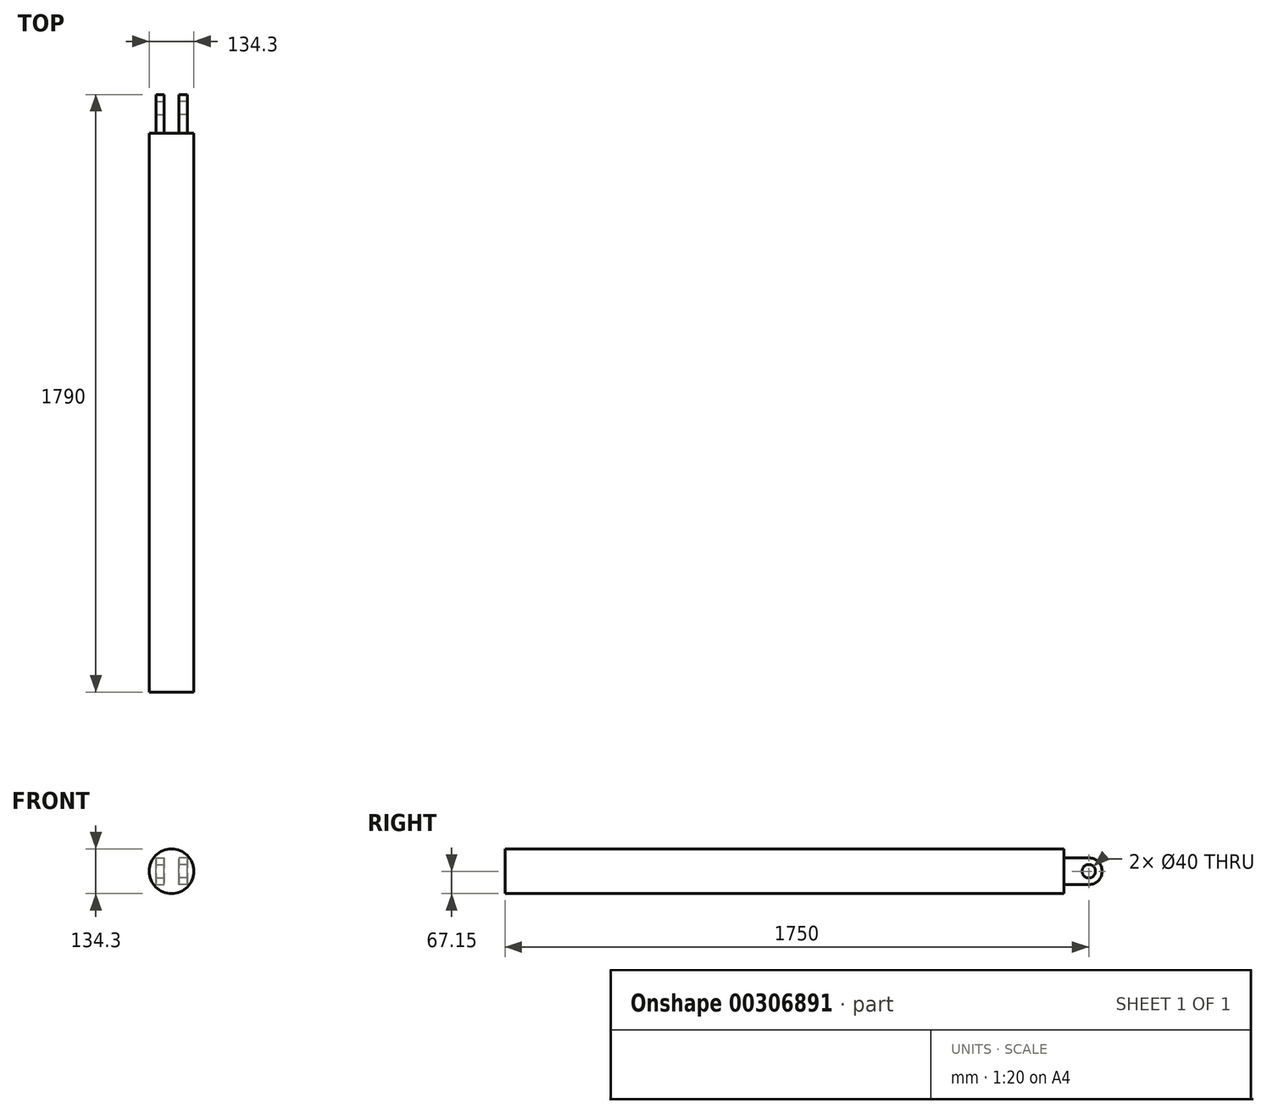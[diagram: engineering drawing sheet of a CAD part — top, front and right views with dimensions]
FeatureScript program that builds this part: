
annotation { "Feature Type Name" : "Feature", "Feature Type Description" : "" }
export const myFeature = defineFeature(function(context is Context, id is Id, definition is map)
    precondition{}
    {
        {
            var Q0;
            Q0=qCreatedBy(makeId("Right.planeOp"),FACE);
            var sketch = newSketch(context, id + "F0", { "sketchPlane" : qUnion([Q0])});
            skCircle(sketch, "E0", {"center": v(0, 0) * mm, "radius": 20 * mm});
            skArc(sketch, "E1", {"start": v(0, -40) * mm, "mid": v(40, 0) * mm, "end": v(0, 40) * mm});
            skLineSegment(sketch, "E2", {"start": v(0, 40) * mm, "end": v(-75, 40) * mm});
            skLineSegment(sketch, "E3", {"start": v(-75, 40) * mm, "end": v(-75, -40) * mm});
            skLineSegment(sketch, "E4", {"start": v(-75, -40) * mm, "end": v(0, -40) * mm});
            skSolve(sketch);
        }
        {
            var Q0;
            Q0=qCreatedBy(makeId("Right.planeOp"),FACE);
            cPlane(context, id + "F1", {"entities" : qUnion([Q0]), "cplaneType" : CPlaneType.OFFSET, "offset" : 22 * mm, "oppositeDirection" : true, "width" : 150 * mm, "height" : 150 * mm});
        }
        {
            var Q0;
            Q0=qCreatedBy(id+"F1.planeOp",FACE);
            var sketch = newSketch(context, id + "F2", { "sketchPlane" : qUnion([Q0])});
            skLineSegment(sketch, "E5.0.0", {"start": v(-75, 40) * mm, "end": v(-75, -40) * mm});
            skLineSegment(sketch, "E5.0.1", {"start": v(-75, -40) * mm, "end": v(0, -40) * mm});
            skArc(sketch, "E5.0.2", {"start": v(0, -40) * mm, "mid": v(40, 0) * mm, "end": v(0, 40) * mm});
            skLineSegment(sketch, "E5.0.3", {"start": v(0, 40) * mm, "end": v(-75, 40) * mm});
            skCircle(sketch, "E6.0", {"center": v(0, 0) * mm, "radius": 20 * mm});
            skSolve(sketch);
        }
        {
            var Q0;
            Q0 = qSketchRegion(id + "F2", true);
            extrude(context, id + "F3", {"entities" : qUnion([Q0]), "oppositeDirection" : true, "depth" : 25 * mm});
        }
        {
            var Q0;
            Q0=qCreatedBy(makeId("Right.planeOp"),FACE);
            var sketch = newSketch(context, id + "F4", { "sketchPlane" : qUnion([Q0])});
            skCircle(sketch, "E7", {"center": v(-1850, 0) * mm, "radius": 20 * mm, "construction": true});
            skCircle(sketch, "E8", {"center": v(-1850, 0) * mm, "radius": 31 * mm, "construction": true});
            skCircle(sketch, "E9.0", {"center": v(0, 0) * mm, "radius": 20 * mm, "construction": true});
            skPoint(sketch, "E10", {"position": v(-1750, 0) * mm});
            skPoint(sketch, "E11", {"position": v(-75, 0) * mm});
            skSolve(sketch);
        }
        {
            var Q0;
            Q0=makeQuery(id+"F3.opExtrude","SWEPT_BODY",BODY,{"disambiguationData":[OSD([sQuery(id+"F2.wireOp",EDGE,"E5.0.0"),sQuery(id+"F2.wireOp",EDGE,"E5.0.1"),sQuery(id+"F2.wireOp",EDGE,"E5.0.2"),sQuery(id+"F2.wireOp",EDGE,"E5.0.3"),sQuery(id+"F2.wireOp",EDGE,"E6.0")])]});
            var Q1;
            Q1=qCreatedBy(makeId("Right.planeOp"),FACE);
            mirror(context, id + "F5", {"entities" : qUnion([Q0]), "mirrorPlane" : qUnion([Q1])});
        }
        {
            var Q0;
            Q0=makeQuery(id+"F5.opPattern","COPY",FACE,{"derivedFrom":makeQuery(id+"F3.opExtrude","SWEPT_FACE",FACE,{"disambiguationData":[OSD([sQuery(id+"F2.wireOp",EDGE,"E5.0.0")])]}),"instanceName":"1"});
            var sketch = newSketch(context, id + "F6", { "sketchPlane" : qUnion([Q0])});
            skCircle(sketch, "E12", {"center": v(0, 0) * mm, "radius": 67.15 * mm});
            skSolve(sketch);
        }
        {
            var Q0;
            Q0 = qSketchRegion(id + "F6", true);
            var Q1;
            Q1=sQuery(id+"F4.wireOp",VERTEX,"E10");
            extrude(context, id + "F7", {"entities" : qUnion([Q0]), "endBound" : BoundingType.UP_TO_VERTEX, "endBoundEntityVertex" : qUnion([Q1]), "depth" : 25 * mm});
        }
    });
